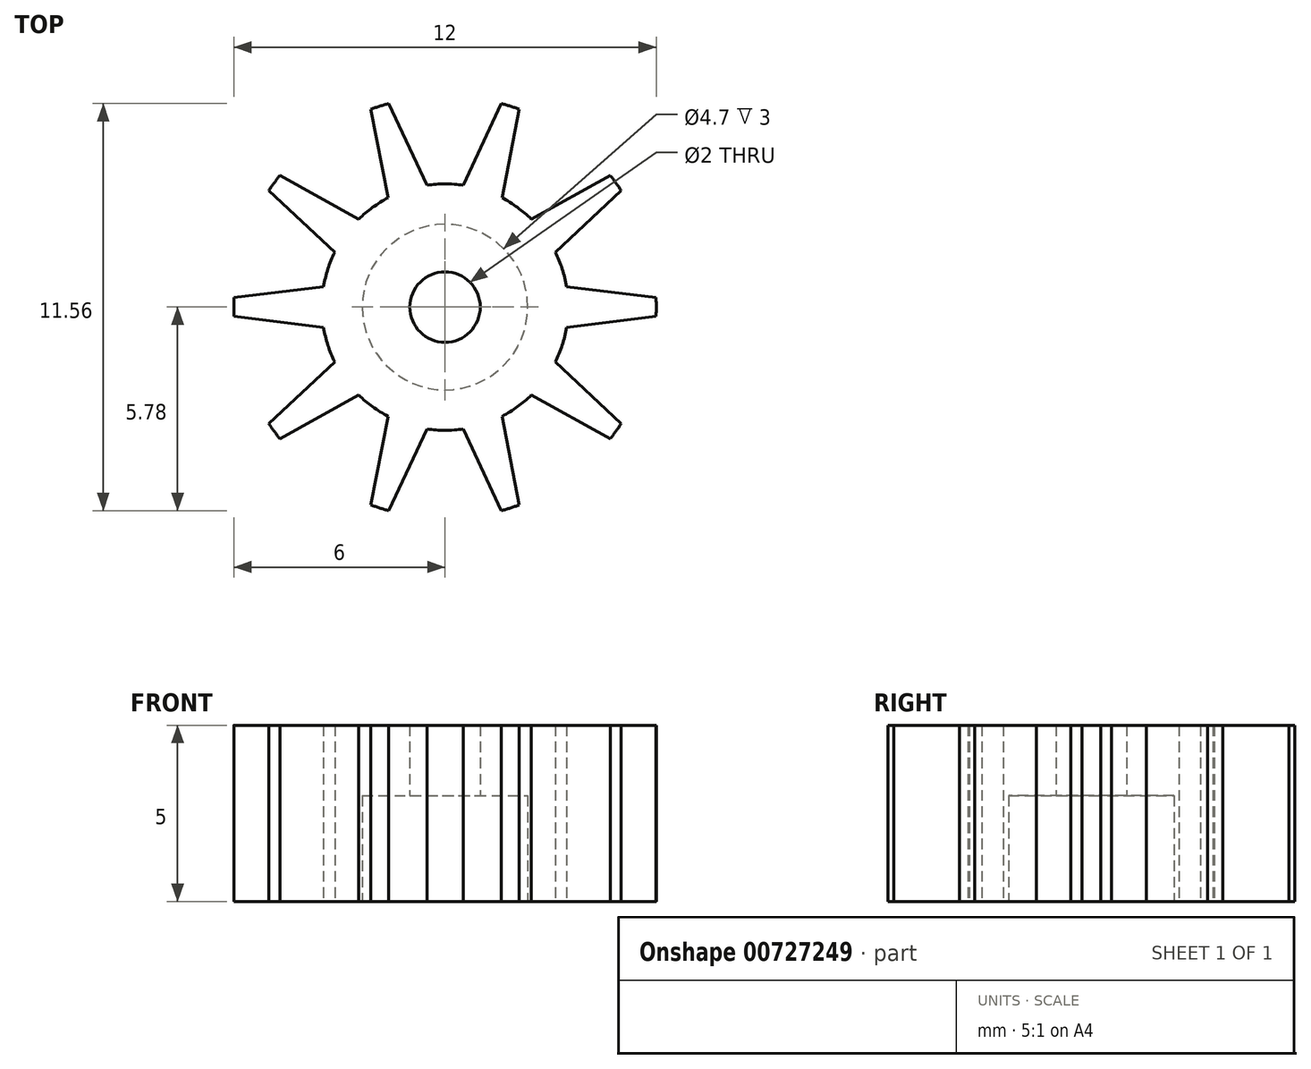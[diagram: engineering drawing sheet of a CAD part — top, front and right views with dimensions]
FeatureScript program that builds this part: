
annotation { "Feature Type Name" : "Feature", "Feature Type Description" : "" }
export const myFeature = defineFeature(function(context is Context, id is Id, definition is map)
    precondition{}
    {
        {
            var Q0;
            Q0=qCreatedBy(makeId("Top.planeOp"),FACE);
            var sketch = newSketch(context, id + "F0", { "sketchPlane" : qUnion([Q0])});
            skCircle(sketch, "E0", {"center": v(0, 0) * mm, "radius": 2.5 * mm});
            skCircle(sketch, "E1", {"center": v(0, 0) * mm, "radius": 6 * mm});
            skSolve(sketch);
        }
        {
            var Q0;
            Q0 = qSketchRegion(id + "F0", true);
            var Q1;
            Q1=makeQuery(id+"F0.imprint","IMPRINT",FACE,{"disambiguationData":[TD([[makeQuery(id+"F0.imprint","IMPRINT",EDGE,{"derivedFrom":sQuery(id+"F0.wireOp",EDGE,"E0")}),1.0]])]});
            extrude(context, id + "F1", {"entities" : qUnion([Q0, Q1]), "depth" : 5 * mm, "offsetDistance" : 25 * mm});
        }
        {
            var Q0;
            Q0=makeQuery(id+"F1.opExtrude","CAP_FACE",FACE,{"disambiguationData":[OSD([sQuery(id+"F0.wireOp",EDGE,"E1")])],"isStart":true});
            var sketch = newSketch(context, id + "F2", { "sketchPlane" : qUnion([Q0])});
            skLineSegment(sketch, "E2", {"start": v(0, 0) * mm, "end": v(0, 10) * mm, "construction": true});
            skLineSegment(sketch, "E3", {"start": v(-1.17, 3.5) * mm, "end": v(1.95, 3.5) * mm, "construction": true});
            skPoint(sketch, "E4", {"position": v(0, 3.5) * mm});
            skCircle(sketch, "E5", {"center": v(0, 0) * mm, "radius": 3.5 * mm});
            skLineSegment(sketch, "E6", {"start": v(0, 2.35) * mm, "end": v(1.6, 5.78) * mm});
            skLineSegment(sketch, "E7", {"start": v(0, 2.35) * mm, "end": v(-1.6, 5.78) * mm});
            skLineSegment(sketch, "E8.1.0", {"start": v(-1.38, 1.9) * mm, "end": v(-4.7, 3.74) * mm});
            skLineSegment(sketch, "E8.1.1", {"start": v(-1.38, 1.9) * mm, "end": v(-2.1, 5.62) * mm});
            skLineSegment(sketch, "E8.2.0", {"start": v(-2.24, 0.73) * mm, "end": v(-6, 0.27) * mm});
            skLineSegment(sketch, "E8.2.1", {"start": v(-2.24, 0.73) * mm, "end": v(-5, 3.3) * mm});
            skLineSegment(sketch, "E8.3.0", {"start": v(-2.24, -0.73) * mm, "end": v(-5, -3.3) * mm});
            skLineSegment(sketch, "E8.3.1", {"start": v(-2.24, -0.73) * mm, "end": v(-6, -0.27) * mm});
            skLineSegment(sketch, "E8.4.0", {"start": v(-1.38, -1.9) * mm, "end": v(-2.1, -5.62) * mm});
            skLineSegment(sketch, "E8.4.1", {"start": v(-1.38, -1.9) * mm, "end": v(-4.7, -3.74) * mm});
            skLineSegment(sketch, "E9.1.5.0", {"start": v(0, -2.35) * mm, "end": v(1.6, -5.78) * mm});
            skLineSegment(sketch, "E9.3.5.0", {"start": v(0, -2.35) * mm, "end": v(-1.6, -5.78) * mm});
            skLineSegment(sketch, "E10.1.6.0", {"start": v(1.38, -1.9) * mm, "end": v(4.7, -3.74) * mm});
            skLineSegment(sketch, "E10.3.6.0", {"start": v(1.38, -1.9) * mm, "end": v(2.1, -5.62) * mm});
            skLineSegment(sketch, "E11.1.7.0", {"start": v(2.24, -0.73) * mm, "end": v(6, -0.27) * mm});
            skLineSegment(sketch, "E11.3.7.0", {"start": v(2.24, -0.73) * mm, "end": v(5, -3.3) * mm});
            skLineSegment(sketch, "E12.1.8.0", {"start": v(2.24, 0.73) * mm, "end": v(5, 3.3) * mm});
            skLineSegment(sketch, "E12.3.8.0", {"start": v(2.24, 0.73) * mm, "end": v(6, 0.27) * mm});
            skLineSegment(sketch, "E13.1.9.0", {"start": v(1.38, 1.9) * mm, "end": v(2.1, 5.62) * mm});
            skLineSegment(sketch, "E13.3.9.0", {"start": v(1.38, 1.9) * mm, "end": v(4.7, 3.74) * mm});
            skSolve(sketch);
        }
        {
            var Q0;
            {var subQ7=sQuery(id+"F2.wireOp",EDGE,"E6");var subQ8=sQuery(id+"F2.wireOp",EDGE,"E5");var subQ9=makeQuery(id+"F2.imprint","INTERSECT",VERTEX,{"derivedFrom":[subQ8,subQ7]});Q0=makeQuery(id+"F2.imprint","IMPRINT",FACE,{"disambiguationData":[TD([[makeQuery(id+"F2.imprint","IMPRINT",EDGE,{"disambiguationData":[TD([[subQ9,-1.0]])],"derivedFrom":subQ8}),-1.0]])]});}
            var Q1;
            {var subQ0=sQuery(id+"F2.wireOp",EDGE,"E7");var subQ1=makeQuery(id+"F1.opExtrude","CAP_EDGE",EDGE,{"disambiguationData":[OSD([sQuery(id+"F0.wireOp",EDGE,"E1")])],"isStart":true});var subQ2=makeQuery(id+"F2.imprint","INTERSECT",VERTEX,{"derivedFrom":[subQ1,subQ0]});Q1=makeQuery(id+"F2.imprint","IMPRINT",FACE,{"disambiguationData":[TD([[makeQuery(id+"F2.imprint","IMPRINT",EDGE,{"disambiguationData":[TD([[subQ2,1.0]])],"derivedFrom":subQ0}),-1.0]])]});}
            var Q2;
            {var subQ1=sQuery(id+"F2.wireOp",EDGE,"E5");var subQ5=sQuery(id+"F2.wireOp",EDGE,"E8.1.1");var subQ6=makeQuery(id+"F2.imprint","INTERSECT",VERTEX,{"derivedFrom":[subQ1,subQ5]});Q2=makeQuery(id+"F2.imprint","IMPRINT",FACE,{"disambiguationData":[TD([[makeQuery(id+"F2.imprint","IMPRINT",EDGE,{"disambiguationData":[TD([[subQ6,-1.0]])],"derivedFrom":subQ1}),-1.0]])]});}
            var Q3;
            {var subQ0=sQuery(id+"F2.wireOp",EDGE,"E8.2.1");var subQ1=sQuery(id+"F2.wireOp",EDGE,"E5");var subQ2=makeQuery(id+"F2.imprint","INTERSECT",VERTEX,{"derivedFrom":[subQ1,subQ0]});Q3=makeQuery(id+"F2.imprint","IMPRINT",FACE,{"disambiguationData":[TD([[makeQuery(id+"F2.imprint","IMPRINT",EDGE,{"disambiguationData":[TD([[subQ2,-1.0]])],"derivedFrom":subQ1}),-1.0]])]});}
            var Q4;
            {var subQ0=sQuery(id+"F2.wireOp",EDGE,"E8.3.1");var subQ1=sQuery(id+"F2.wireOp",EDGE,"E5");var subQ2=makeQuery(id+"F2.imprint","INTERSECT",VERTEX,{"derivedFrom":[subQ1,subQ0]});Q4=makeQuery(id+"F2.imprint","IMPRINT",FACE,{"disambiguationData":[TD([[makeQuery(id+"F2.imprint","IMPRINT",EDGE,{"disambiguationData":[TD([[subQ2,-1.0]])],"derivedFrom":subQ1}),-1.0]])]});}
            var Q5;
            {var subQ0=sQuery(id+"F2.wireOp",EDGE,"E8.4.1");var subQ1=sQuery(id+"F2.wireOp",EDGE,"E5");var subQ2=makeQuery(id+"F2.imprint","INTERSECT",VERTEX,{"derivedFrom":[subQ1,subQ0]});Q5=makeQuery(id+"F2.imprint","IMPRINT",FACE,{"disambiguationData":[TD([[makeQuery(id+"F2.imprint","IMPRINT",EDGE,{"disambiguationData":[TD([[subQ2,-1.0]])],"derivedFrom":subQ1}),-1.0]])]});}
            var Q6;
            {var subQ1=sQuery(id+"F2.wireOp",EDGE,"E5");var subQ8=sQuery(id+"F2.wireOp",EDGE,"E9.3.5.0");var subQ10=makeQuery(id+"F2.imprint","INTERSECT",VERTEX,{"derivedFrom":[subQ1,subQ8]});Q6=makeQuery(id+"F2.imprint","IMPRINT",FACE,{"disambiguationData":[TD([[makeQuery(id+"F2.imprint","IMPRINT",EDGE,{"disambiguationData":[TD([[subQ10,-1.0]])],"derivedFrom":subQ1}),-1.0]])]});}
            var Q7;
            {var subQ0=sQuery(id+"F2.wireOp",EDGE,"E10.3.6.0");var subQ1=sQuery(id+"F2.wireOp",EDGE,"E5");var subQ2=makeQuery(id+"F2.imprint","INTERSECT",VERTEX,{"derivedFrom":[subQ1,subQ0]});Q7=makeQuery(id+"F2.imprint","IMPRINT",FACE,{"disambiguationData":[TD([[makeQuery(id+"F2.imprint","IMPRINT",EDGE,{"disambiguationData":[TD([[subQ2,-1.0]])],"derivedFrom":subQ1}),-1.0]])]});}
            var Q8;
            {var subQ0=sQuery(id+"F2.wireOp",EDGE,"E11.3.7.0");var subQ1=sQuery(id+"F2.wireOp",EDGE,"E5");var subQ2=makeQuery(id+"F2.imprint","INTERSECT",VERTEX,{"derivedFrom":[subQ1,subQ0]});Q8=makeQuery(id+"F2.imprint","IMPRINT",FACE,{"disambiguationData":[TD([[makeQuery(id+"F2.imprint","IMPRINT",EDGE,{"disambiguationData":[TD([[subQ2,-1.0]])],"derivedFrom":subQ1}),-1.0]])]});}
            var Q9;
            {var subQ1=sQuery(id+"F2.wireOp",EDGE,"E5");var subQ5=sQuery(id+"F2.wireOp",EDGE,"E12.1.8.0");var subQ6=makeQuery(id+"F2.imprint","INTERSECT",VERTEX,{"derivedFrom":[subQ1,subQ5]});Q9=makeQuery(id+"F2.imprint","IMPRINT",FACE,{"disambiguationData":[TD([[makeQuery(id+"F2.imprint","IMPRINT",EDGE,{"disambiguationData":[TD([[subQ6,1.0]])],"derivedFrom":subQ1}),-1.0]])]});}
            var Q10;
            {var subQ1=sQuery(id+"F2.wireOp",EDGE,"E5");var subQ8=sQuery(id+"F2.wireOp",EDGE,"E13.3.9.0");var subQ11=makeQuery(id+"F2.imprint","INTERSECT",VERTEX,{"derivedFrom":[subQ1,subQ8]});Q10=makeQuery(id+"F2.imprint","IMPRINT",FACE,{"disambiguationData":[TD([[makeQuery(id+"F2.imprint","IMPRINT",EDGE,{"disambiguationData":[TD([[subQ11,-1.0]])],"derivedFrom":subQ1}),-1.0]])]});}
            var Q11;
            {var subQ0=sQuery(id+"F2.wireOp",EDGE,"E6");var subQ1=makeQuery(id+"F1.opExtrude","CAP_EDGE",EDGE,{"disambiguationData":[OSD([sQuery(id+"F0.wireOp",EDGE,"E1")])],"isStart":true});var subQ2=makeQuery(id+"F2.imprint","INTERSECT",VERTEX,{"derivedFrom":[subQ1,subQ0]});Q11=makeQuery(id+"F2.imprint","IMPRINT",FACE,{"disambiguationData":[TD([[makeQuery(id+"F2.imprint","IMPRINT",EDGE,{"disambiguationData":[TD([[subQ2,1.0]])],"derivedFrom":subQ0}),1.0]])]});}
            var Q12;
            {var subQ0=sQuery(id+"F2.wireOp",EDGE,"E12.1.8.0");var subQ1=makeQuery(id+"F1.opExtrude","CAP_EDGE",EDGE,{"disambiguationData":[OSD([sQuery(id+"F0.wireOp",EDGE,"E1")])],"isStart":true});var subQ2=makeQuery(id+"F2.imprint","INTERSECT",VERTEX,{"derivedFrom":[subQ1,subQ0]});Q12=makeQuery(id+"F2.imprint","IMPRINT",FACE,{"disambiguationData":[TD([[makeQuery(id+"F2.imprint","IMPRINT",EDGE,{"disambiguationData":[TD([[subQ2,1.0]])],"derivedFrom":subQ0}),-1.0]])]});}
            var Q13;
            {var subQ0=sQuery(id+"F2.wireOp",EDGE,"E11.1.7.0");var subQ1=makeQuery(id+"F1.opExtrude","CAP_EDGE",EDGE,{"disambiguationData":[OSD([sQuery(id+"F0.wireOp",EDGE,"E1")])],"isStart":true});var subQ2=makeQuery(id+"F2.imprint","INTERSECT",VERTEX,{"derivedFrom":[subQ1,subQ0]});Q13=makeQuery(id+"F2.imprint","IMPRINT",FACE,{"disambiguationData":[TD([[makeQuery(id+"F2.imprint","IMPRINT",EDGE,{"disambiguationData":[TD([[subQ2,1.0]])],"derivedFrom":subQ0}),-1.0]])]});}
            var Q14;
            {var subQ0=sQuery(id+"F2.wireOp",EDGE,"E10.1.6.0");var subQ1=makeQuery(id+"F1.opExtrude","CAP_EDGE",EDGE,{"disambiguationData":[OSD([sQuery(id+"F0.wireOp",EDGE,"E1")])],"isStart":true});var subQ2=makeQuery(id+"F2.imprint","INTERSECT",VERTEX,{"derivedFrom":[subQ1,subQ0]});Q14=makeQuery(id+"F2.imprint","IMPRINT",FACE,{"disambiguationData":[TD([[makeQuery(id+"F2.imprint","IMPRINT",EDGE,{"disambiguationData":[TD([[subQ2,1.0]])],"derivedFrom":subQ0}),-1.0]])]});}
            var Q15;
            {var subQ0=sQuery(id+"F2.wireOp",EDGE,"E9.1.5.0");var subQ1=makeQuery(id+"F1.opExtrude","CAP_EDGE",EDGE,{"disambiguationData":[OSD([sQuery(id+"F0.wireOp",EDGE,"E1")])],"isStart":true});var subQ2=makeQuery(id+"F2.imprint","INTERSECT",VERTEX,{"derivedFrom":[subQ1,subQ0]});Q15=makeQuery(id+"F2.imprint","IMPRINT",FACE,{"disambiguationData":[TD([[makeQuery(id+"F2.imprint","IMPRINT",EDGE,{"disambiguationData":[TD([[subQ2,1.0]])],"derivedFrom":subQ0}),-1.0]])]});}
            var Q16;
            {var subQ0=sQuery(id+"F2.wireOp",EDGE,"E8.4.0");var subQ1=makeQuery(id+"F1.opExtrude","CAP_EDGE",EDGE,{"disambiguationData":[OSD([sQuery(id+"F0.wireOp",EDGE,"E1")])],"isStart":true});var subQ2=makeQuery(id+"F2.imprint","INTERSECT",VERTEX,{"derivedFrom":[subQ1,subQ0]});Q16=makeQuery(id+"F2.imprint","IMPRINT",FACE,{"disambiguationData":[TD([[makeQuery(id+"F2.imprint","IMPRINT",EDGE,{"disambiguationData":[TD([[subQ2,1.0]])],"derivedFrom":subQ0}),-1.0]])]});}
            var Q17;
            {var subQ0=sQuery(id+"F2.wireOp",EDGE,"E8.3.0");var subQ1=makeQuery(id+"F1.opExtrude","CAP_EDGE",EDGE,{"disambiguationData":[OSD([sQuery(id+"F0.wireOp",EDGE,"E1")])],"isStart":true});var subQ2=makeQuery(id+"F2.imprint","INTERSECT",VERTEX,{"derivedFrom":[subQ1,subQ0]});Q17=makeQuery(id+"F2.imprint","IMPRINT",FACE,{"disambiguationData":[TD([[makeQuery(id+"F2.imprint","IMPRINT",EDGE,{"disambiguationData":[TD([[subQ2,1.0]])],"derivedFrom":subQ0}),-1.0]])]});}
            var Q18;
            {var subQ0=sQuery(id+"F2.wireOp",EDGE,"E8.2.0");var subQ1=makeQuery(id+"F1.opExtrude","CAP_EDGE",EDGE,{"disambiguationData":[OSD([sQuery(id+"F0.wireOp",EDGE,"E1")])],"isStart":true});var subQ2=makeQuery(id+"F2.imprint","INTERSECT",VERTEX,{"derivedFrom":[subQ1,subQ0]});Q18=makeQuery(id+"F2.imprint","IMPRINT",FACE,{"disambiguationData":[TD([[makeQuery(id+"F2.imprint","IMPRINT",EDGE,{"disambiguationData":[TD([[subQ2,1.0]])],"derivedFrom":subQ0}),-1.0]])]});}
            var Q19;
            {var subQ0=sQuery(id+"F2.wireOp",EDGE,"E8.1.0");var subQ1=makeQuery(id+"F1.opExtrude","CAP_EDGE",EDGE,{"disambiguationData":[OSD([sQuery(id+"F0.wireOp",EDGE,"E1")])],"isStart":true});var subQ2=makeQuery(id+"F2.imprint","INTERSECT",VERTEX,{"derivedFrom":[subQ1,subQ0]});Q19=makeQuery(id+"F2.imprint","IMPRINT",FACE,{"disambiguationData":[TD([[makeQuery(id+"F2.imprint","IMPRINT",EDGE,{"disambiguationData":[TD([[subQ2,1.0]])],"derivedFrom":subQ0}),-1.0]])]});}
            extrude(context, id + "F3", {"entities" : qUnion([Q0, Q1, Q2, Q3, Q4, Q5, Q6, Q7, Q8, Q9, Q10, Q11, Q12, Q13, Q14, Q15, Q16, Q17, Q18, Q19]), "operationType" : NewBodyOperationType.REMOVE, "oppositeDirection" : true, "depth" : 25 * mm, "offsetDistance" : 25 * mm});
        }
        {
            var Q0;
            Q0=makeQuery(id+"F1.opExtrude","CAP_FACE",FACE,{"disambiguationData":[OSD([sQuery(id+"F0.wireOp",EDGE,"E1")])],"isStart":true});
            var sketch = newSketch(context, id + "F4", { "sketchPlane" : qUnion([Q0])});
            skCircle(sketch, "E14", {"center": v(0, 0) * mm, "radius": 2.35 * mm});
            skSolve(sketch);
        }
        {
            var Q0;
            Q0=makeQuery(id+"F4.imprint","IMPRINT",FACE,{"disambiguationData":[TD([[makeQuery(id+"F4.imprint","IMPRINT",EDGE,{"derivedFrom":sQuery(id+"F4.wireOp",EDGE,"E14")}),1.0]])]});
            extrude(context, id + "F5", {"entities" : qUnion([Q0]), "operationType" : NewBodyOperationType.REMOVE, "oppositeDirection" : true, "depth" : 3 * mm, "offsetDistance" : 25 * mm});
        }
        {
            var Q0;
            Q0=makeQuery(id+"F1.opExtrude","CAP_FACE",FACE,{"disambiguationData":[OSD([sQuery(id+"F0.wireOp",EDGE,"E1")])],"isStart":true});
            var sketch = newSketch(context, id + "F6", { "sketchPlane" : qUnion([Q0])});
            skCircle(sketch, "E15", {"center": v(0, 0) * mm, "radius": 1 * mm});
            skSolve(sketch);
        }
        {
            var Q0;
            Q0 = qSketchRegion(id + "F6", true);
            extrude(context, id + "F7", {"entities" : qUnion([Q0]), "operationType" : NewBodyOperationType.REMOVE, "oppositeDirection" : true, "depth" : 25 * mm, "offsetDistance" : 25 * mm});
        }
    });
